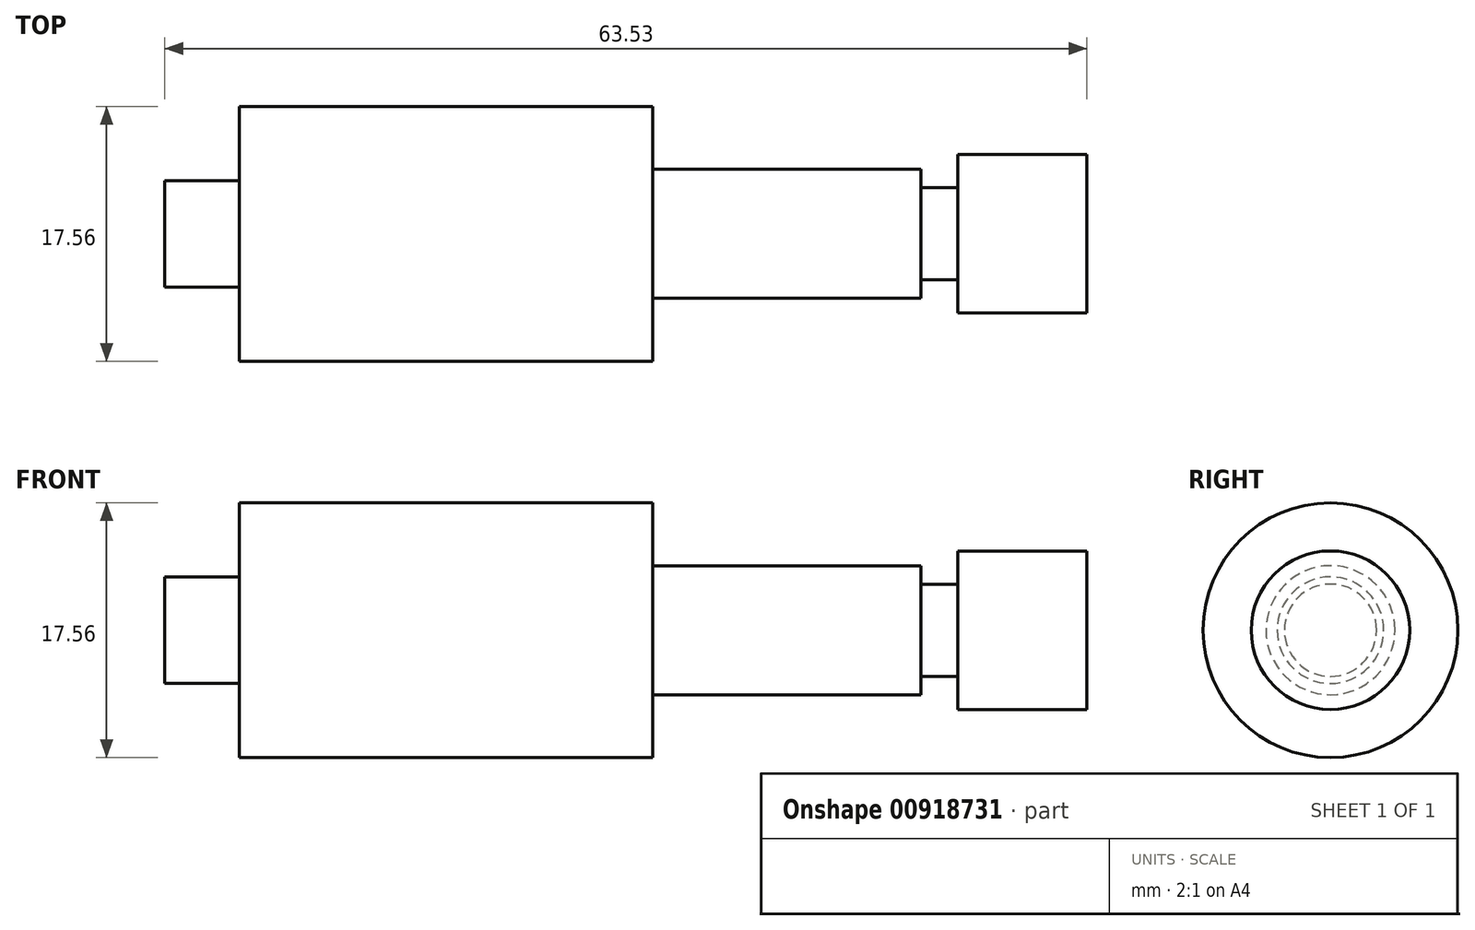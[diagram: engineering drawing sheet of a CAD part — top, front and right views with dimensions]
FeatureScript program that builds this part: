
annotation { "Feature Type Name" : "Feature", "Feature Type Description" : "" }
export const myFeature = defineFeature(function(context is Context, id is Id, definition is map)
    precondition{}
    {
        {
            var Q0;
            Q0=qCreatedBy(makeId("Top.planeOp"),FACE);
            var sketch = newSketch(context, id + "F0", { "sketchPlane" : qUnion([Q0])});
            skLineSegment(sketch, "E0.top", {"start": v(-155.9, 5.46) * mm, "end": v(-147, 5.46) * mm});
            skLineSegment(sketch, "E1.bottom", {"start": v(-155.9, 3.18) * mm, "end": v(-158.44, 3.18) * mm});
            skLineSegment(sketch, "E2.bottom", {"start": v(-158.44, 4.45) * mm, "end": v(-176.94, 4.45) * mm});
            skLineSegment(sketch, "E2.left", {"start": v(-158.44, 4.45) * mm, "end": v(-158.44, 3.18) * mm});
            skLineSegment(sketch, "E3.trimOffspring", {"start": v(-155.9, 3.18) * mm, "end": v(-155.9, 5.46) * mm});
            skLineSegment(sketch, "E4.top", {"start": v(-176.94, 8.78) * mm, "end": v(-205.4, 8.78) * mm});
            skLineSegment(sketch, "E5.top", {"start": v(-205.4, 3.67) * mm, "end": v(-210.54, 3.67) * mm});
            skLineSegment(sketch, "E6.trimOffspring", {"start": v(-176.94, 4.45) * mm, "end": v(-176.94, 8.78) * mm});
            skLineSegment(sketch, "E7.trimOffspring", {"start": v(-205.4, 3.67) * mm, "end": v(-205.4, 8.78) * mm});
            skLineSegment(sketch, "E8", {"start": v(-147, 0) * mm, "end": v(-210.54, 0) * mm});
            skLineSegment(sketch, "E9", {"start": v(-147, 5.46) * mm, "end": v(-147, 0) * mm});
            skLineSegment(sketch, "E10", {"start": v(-210.54, 3.67) * mm, "end": v(-210.54, 0) * mm});
            skSolve(sketch);
        }
        {
            var Q0;
            Q0=makeQuery(id+"F0.imprint","IMPRINT",FACE,{"disambiguationData":[TD([[makeQuery(id+"F0.imprint","IMPRINT",EDGE,{"derivedFrom":sQuery(id+"F0.wireOp",EDGE,"E0.top")}),-1.0]])]});
            var Q1;
            Q1=sQuery(id+"F0.wireOp",EDGE,"E8");
            revolve(context, id + "F1", {"surfaceOperationType" : NewSurfaceOperationType.NEW, "entities" : qUnion([Q0]), "axis" : qUnion([Q1]), "revolveType" : RevolveType.FULL});
        }
    });
